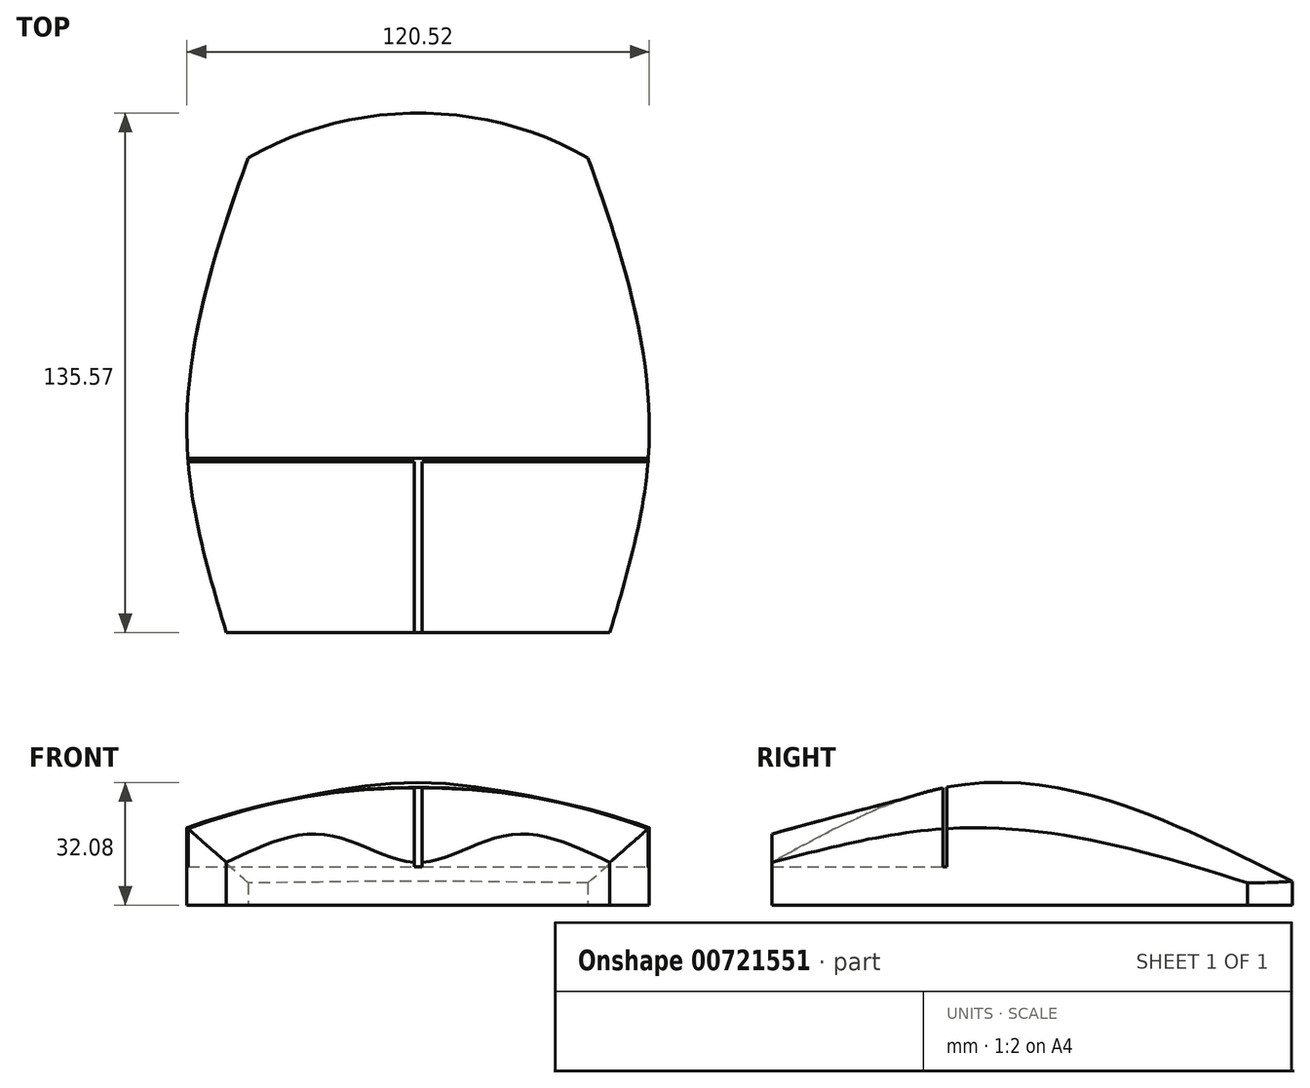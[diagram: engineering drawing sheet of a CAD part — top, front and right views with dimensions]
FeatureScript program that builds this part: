
annotation { "Feature Type Name" : "Feature", "Feature Type Description" : "" }
export const myFeature = defineFeature(function(context is Context, id is Id, definition is map)
    precondition{}
    {
        {
            var Q0;
            Q0=qCreatedBy(makeId("Front.planeOp"),FACE);
            var sketch = newSketch(context, id + "F0", { "sketchPlane" : qUnion([Q0])});
            skLineSegment(sketch, "E0", {"start": v(-40, 0) * mm, "end": v(40, 0) * mm});
            skLineSegment(sketch, "E1", {"start": v(40, 0) * mm, "end": v(40, 2) * mm});
            skLineSegment(sketch, "E2", {"start": v(-40, 0) * mm, "end": v(-40, 2) * mm});
            skArc(sketch, "E3", {"start": v(40, 2) * mm, "mid": v(0, 6.2) * mm, "end": v(-40, 2) * mm});
            skPoint(sketch, "E4", {"position": v(0, 0) * mm});
            skSolve(sketch);
        }
        {
            var Q0;
            Q0=qCreatedBy(makeId("Right.planeOp"),FACE);
            var sketch = newSketch(context, id + "F1", { "sketchPlane" : qUnion([Q0])});
            skLineSegment(sketch, "E5", {"start": v(0, 0) * mm, "end": v(-90, 0) * mm, "construction": true});
            skSolve(sketch);
        }
        {
            var Q0;
            Q0=sQuery(id+"F1.wireOp",VERTEX,"E5.end");
            var Q1;
            Q1=sQuery(id+"F1.wireOp",EDGE,"E5");
            cPlane(context, id + "F2", {"entities" : qUnion([Q0, Q1]), "cplaneType" : CPlaneType.LINE_POINT, "offset" : 25 * mm, "width" : 150 * mm, "height" : 150 * mm});
        }
        {
            var Q0;
            Q0=qCreatedBy(id+"F2.planeOp",FACE);
            var sketch = newSketch(context, id + "F3", { "sketchPlane" : qUnion([Q0])});
            skLineSegment(sketch, "E6", {"start": v(-60, 0) * mm, "end": v(60, 0) * mm});
            skLineSegment(sketch, "E7", {"start": v(60, 0) * mm, "end": v(60, 20) * mm});
            skLineSegment(sketch, "E8", {"start": v(-60, 0) * mm, "end": v(-60, 20) * mm});
            skPoint(sketch, "E9", {"position": v(0, 0) * mm});
            skArc(sketch, "E10", {"start": v(60, 20) * mm, "mid": v(0, 30.81) * mm, "end": v(-60, 20) * mm});
            skSolve(sketch);
        }
        {
            var Q0;
            Q0=qCreatedBy(makeId("Top.planeOp"),FACE);
            var sketch = newSketch(context, id + "F4", { "sketchPlane" : qUnion([Q0])});
            skLineSegment(sketch, "E11", {"start": v(0, -89.53) * mm, "end": v(0, -135.57) * mm, "construction": true});
            skSolve(sketch);
        }
        {
            var Q0;
            Q0=sQuery(id+"F4.wireOp",VERTEX,"E11.end");
            var Q1;
            Q1=sQuery(id+"F4.wireOp",EDGE,"E11");
            cPlane(context, id + "F5", {"entities" : qUnion([Q0, Q1]), "cplaneType" : CPlaneType.LINE_POINT, "offset" : 25 * mm, "width" : 150 * mm, "height" : 150 * mm});
        }
        {
            var Q0;
            Q0=qCreatedBy(id+"F5.planeOp",FACE);
            var sketch = newSketch(context, id + "F6", { "sketchPlane" : qUnion([Q0])});
            skLineSegment(sketch, "E12", {"start": v(-50, 0) * mm, "end": v(50, 0) * mm});
            skLineSegment(sketch, "E13", {"start": v(50, 0) * mm, "end": v(50, 11.2) * mm});
            skLineSegment(sketch, "E14", {"start": v(-50, 0) * mm, "end": v(-50, 11.2) * mm});
            skPoint(sketch, "E15", {"position": v(0, 0) * mm});
            skLineSegment(sketch, "E16", {"start": v(0, 0) * mm, "end": v(0, 11.2) * mm, "construction": true});
            skPoint(sketch, "E17", {"position": v(-25, 0) * mm});
            skPoint(sketch, "E18", {"position": v(25, 0) * mm});
            skFitSpline(sketch, "E19", {"points": [v(-50, 11.2) * mm, v(-25, 18.52) * mm, v(0, 11.2) * mm, v(25, 18.52) * mm, v(50, 11.2) * mm], "startDerivative": vector(84, 38.69) * mm, "endDerivative": vector(84, -38.69) * mm});
            skSolve(sketch);
        }
        {
            var Q0;
            Q0=makeQuery(id+"F0.imprint","IMPRINT",FACE,{"disambiguationData":[TD([[makeQuery(id+"F0.imprint","IMPRINT",EDGE,{"derivedFrom":sQuery(id+"F0.wireOp",EDGE,"E0")}),1.0]])]});
            var Q1;
            Q1=makeQuery(id+"F3.imprint","IMPRINT",FACE,{"disambiguationData":[TD([[makeQuery(id+"F3.imprint","IMPRINT",EDGE,{"derivedFrom":sQuery(id+"F3.wireOp",EDGE,"E6")}),1.0]])]});
            var Q2;
            Q2=makeQuery(id+"F6.imprint","IMPRINT",FACE,{"disambiguationData":[TD([[makeQuery(id+"F6.imprint","IMPRINT",EDGE,{"derivedFrom":sQuery(id+"F6.wireOp",EDGE,"E12")}),1.0]])]});
            loft(context, id + "F7", {"sheetProfilesArray" : [{ "sheetProfileEntities" : qUnion([Q0]) }, { "sheetProfileEntities" : qUnion([Q1]) }, { "sheetProfileEntities" : qUnion([Q2]) }]});
        }
        {
            var Q0;
            Q0=makeQuery(id+"F7.opLoft","SWEPT_FACE",FACE,{"disambiguationData":[OSD([sQuery(id+"F0.wireOp",EDGE,"E0"),sQuery(id+"F0.wireOp",EDGE,"E1"),sQuery(id+"F0.wireOp",EDGE,"E2"),sQuery(id+"F3.wireOp",EDGE,"E6"),sQuery(id+"F3.wireOp",EDGE,"E7"),sQuery(id+"F3.wireOp",EDGE,"E8")])]});
            var sketch = newSketch(context, id + "F8", { "sketchPlane" : qUnion([Q0])});
            skArc(sketch, "E20", {"start": v(-44.26, 11.64) * mm, "mid": v(0, 0) * mm, "end": v(44.26, 11.64) * mm});
            skSolve(sketch);
        }
        {
            var Q0;
            {var subQ0=sQuery(id+"F8.wireOp",EDGE,"E20");var subQ1=sQuery(id+"F0.wireOp",EDGE,"E1");var subQ2=sQuery(id+"F0.wireOp",EDGE,"E0");var subQ5=makeQuery(id+"F7.opLoft","MID_CAP_EDGE",EDGE,{"disambiguationData":[OSD([subQ2,subQ1,sQuery(id+"F0.wireOp",EDGE,"E2")])],"capPos":0.0});var subQ6=makeQuery(id+"F8.imprint","INTERSECT",VERTEX,{"derivedFrom":[subQ5,subQ0]});Q0=makeQuery(id+"F8.imprint","IMPRINT",FACE,{"disambiguationData":[TD([[makeQuery(id+"F8.imprint","IMPRINT",EDGE,{"disambiguationData":[TD([[subQ6,-1.0]])],"derivedFrom":subQ0}),-1.0]])]});}
            var Q1;
            {var subQ0=sQuery(id+"F8.wireOp",EDGE,"E20");var subQ1=sQuery(id+"F0.wireOp",EDGE,"E2");var subQ2=sQuery(id+"F0.wireOp",EDGE,"E0");var subQ5=makeQuery(id+"F7.opLoft","MID_CAP_EDGE",EDGE,{"disambiguationData":[OSD([subQ2,sQuery(id+"F0.wireOp",EDGE,"E1"),subQ1])],"capPos":0.0});var subQ6=makeQuery(id+"F8.imprint","INTERSECT",VERTEX,{"derivedFrom":[subQ5,subQ0]});Q1=makeQuery(id+"F8.imprint","IMPRINT",FACE,{"disambiguationData":[TD([[makeQuery(id+"F8.imprint","IMPRINT",EDGE,{"disambiguationData":[TD([[subQ6,1.0]])],"derivedFrom":subQ0}),-1.0]])]});}
            extrude(context, id + "F9", {"entities" : qUnion([Q0, Q1]), "operationType" : NewBodyOperationType.REMOVE, "oppositeDirection" : true, "depth" : 25 * mm, "offsetDistance" : 25 * mm, "hasSecondDirection" : true, "secondDirectionOppositeDirection" : false, "secondDirectionDepth" : 25 * mm});
        }
        {
            var Q0;
            Q0=qCreatedBy(makeId("Top.planeOp"),FACE);
            cPlane(context, id + "F10", {"entities" : qUnion([Q0]), "cplaneType" : CPlaneType.OFFSET, "offset" : 10 * mm, "width" : 150 * mm, "height" : 150 * mm});
        }
        {
            var Q0;
            Q0=qCreatedBy(id+"F10.planeOp",FACE);
            var sketch = newSketch(context, id + "F11", { "sketchPlane" : qUnion([Q0])});
            skLineSegment(sketch, "E21.bottom", {"start": v(-71.37, -90) * mm, "end": v(78.63, -90) * mm});
            skLineSegment(sketch, "E21.top", {"start": v(-71.37, -91) * mm, "end": v(-1, -91) * mm});
            skLineSegment(sketch, "E21.left", {"start": v(-71.37, -90) * mm, "end": v(-71.37, -91) * mm});
            skLineSegment(sketch, "E21.right", {"start": v(78.63, -90) * mm, "end": v(78.63, -91) * mm});
            skLineSegment(sketch, "E22", {"start": v(1, -91) * mm, "end": v(1, -140.47) * mm});
            skLineSegment(sketch, "E23", {"start": v(1, -140.47) * mm, "end": v(-1, -140.47) * mm});
            skLineSegment(sketch, "E24", {"start": v(-1, -140.47) * mm, "end": v(-1, -91) * mm});
            skLineSegment(sketch, "E25.trimOffspring", {"start": v(1, -91) * mm, "end": v(78.63, -91) * mm});
            skSolve(sketch);
        }
        {
            var Q0;
            Q0=makeQuery(id+"F11.imprint","IMPRINT",FACE,{"disambiguationData":[TD([[makeQuery(id+"F11.imprint","IMPRINT",EDGE,{"derivedFrom":sQuery(id+"F11.wireOp",EDGE,"E21.bottom")}),-1.0]])]});
            extrude(context, id + "F12", {"entities" : qUnion([Q0]), "operationType" : NewBodyOperationType.REMOVE, "depth" : 25 * mm, "offsetDistance" : 25 * mm});
        }
    });
